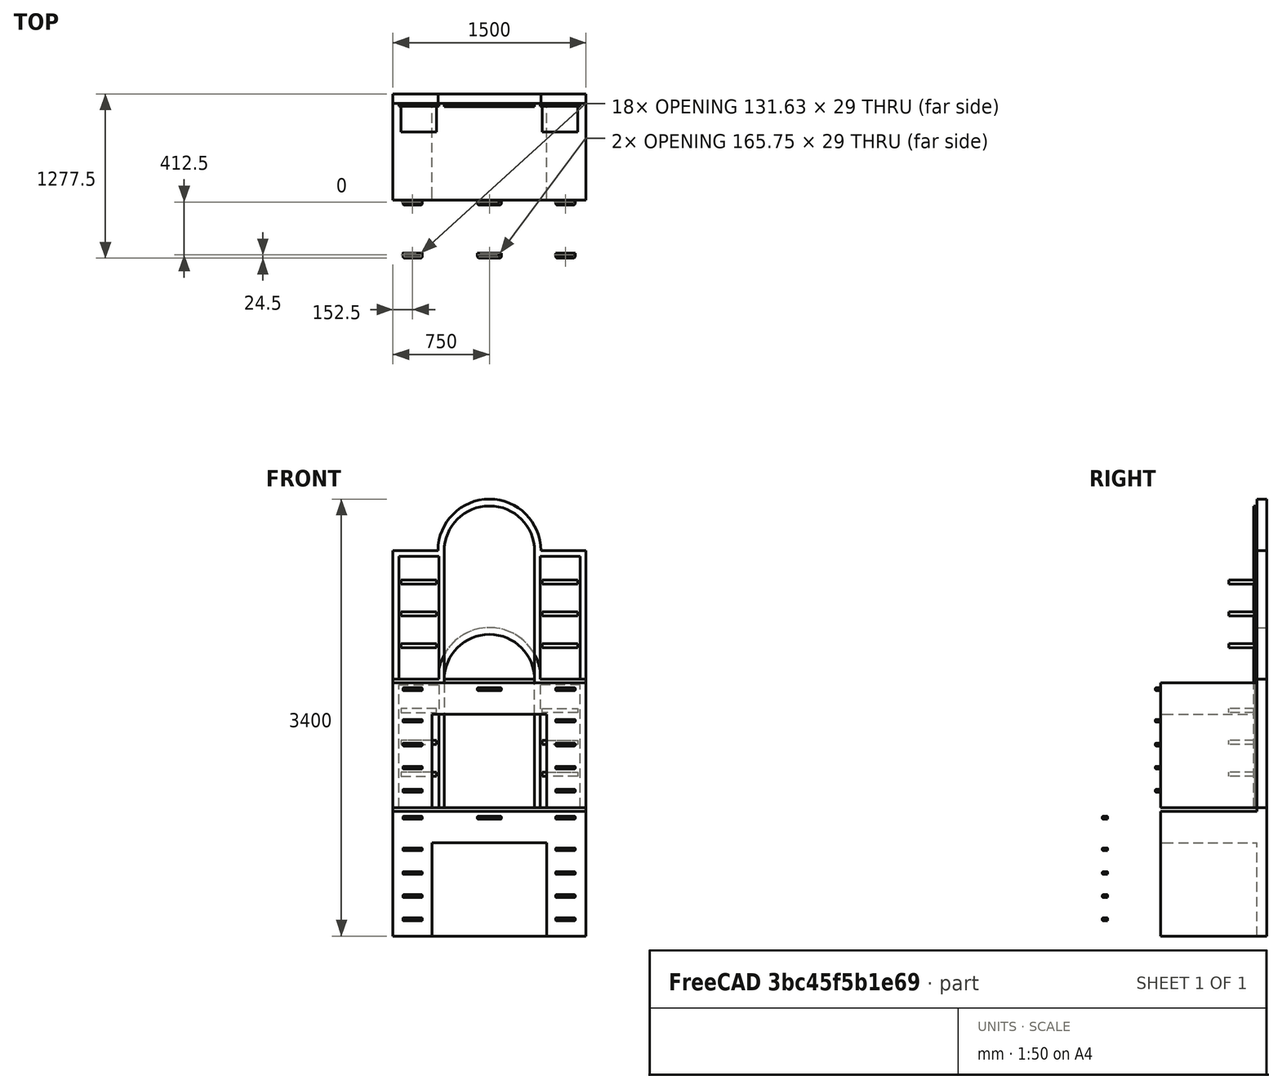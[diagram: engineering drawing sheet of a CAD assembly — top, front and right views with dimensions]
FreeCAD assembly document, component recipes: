
FREECAD ASSEMBLY — COMPONENT RECIPES ("Dressing_Table")

This assembly document has 3 components, labeled P0..P2 below (a component is one placed body or linked part). 3 of them carry a construction recipe — the FreeCAD feature program that regenerates the part from scratch, quoted from this document or its linked companion documents; the rest are supplied as boundary geometry only. No exploded tour is included for this assembly.
COMPONENT P0 — recipe-attached ("Body013", modeled in this document).
Construction recipe (the document's own serialized feature program — sketch geometry with constraints, then the solid features built on it; lengths are millimeters unless a unit is written):

FEATURE [PartDesign::ShapeBinder] CopyPad005
  Placement = pos=(0,-20,9e-15) rot=(0,0,1;0rad)
  TraceSupport = false
FEATURE [PartDesign::Plane] DatumPlane011
  AttachmentSupport = -> [CopyPad005]
  Length = 899.662
  MapMode = 5
  Placement = pos=(0,-95,2.55e-14) rot=(1,0,0;1.5708rad)
  ResizeMode = 0
  Width = 1568.05
FEATURE [Sketcher::SketchObject] Sketch030
  ArcFitTolerance = 1e-06
  AttachmentSupport = -> [CopyPad005]
  ExternalGeometry = -> [CopyPad005]
  FullyConstrained = false
  MakeInternals = false
  MapMode = 5
  Placement = pos=(0,-95,2.55e-14) rot=(1,0,0;1.5708rad)
  sketch-geometry (4):
    g0: LineSegment StartX=-351.618 StartY=995.137 StartZ=0 EndX=-351.618 EndY=0 EndZ=0
    g1: LineSegment StartX=-351.618 StartY=0 StartZ=0 EndX=351.618 EndY=0 EndZ=0
    g2: LineSegment StartX=351.618 StartY=0 StartZ=0 EndX=351.618 EndY=995.137 EndZ=0
    g3: ArcOfCircle CenterX=1.05374e-11 CenterY=995.137 CenterZ=0 NormalX=0 NormalY=0 NormalZ=1 AngleXU=0 Radius=351.618 StartAngle=8.98854e-10 EndAngle=3.14159
  constraints (10):
    c: Coincident(g0,g1)
    c: Coincident(g1,g2)
    c: Vertical(g0)
    c: Vertical(g2)
    c: Horizontal(g1)
    c: Coincident(g0,g-4)
    c: Coincident(g1,g-3)
    c: Coincident(g3,g0)
    c: Coincident(g3,g2)
    c: Tangent(g3,g-5)
FEATURE [PartDesign::Pad] Pad017
  Direction = (0,-1,2e-16)
  Length = 5
  Length2 = 10
  Placement = pos=(0,-20,9e-15) rot=(0,0,1;0rad)
  Profile = -> Sketch030
  ReferenceAxis = -> Sketch030 [N_Axis]
  Refine = true
  Suppressed = false
  Type = 0
FEATURE [PartDesign::Body] Body012
  AllowCompound = false
  Group = -> [DatumPlane011,CopyPad005,Sketch030,Pad017]
  Origin = -> Origin020
  Placement = pos=(0,412.5,0) rot=(0,0,1;0rad)
  Tip = -> Pad017
COMPONENT P1 — recipe-attached ("dressing_table002", modeled in this document).
Construction recipe (the document's own serialized feature program — sketch geometry with constraints, then the solid features built on it; lengths are millimeters unless a unit is written):

FEATURE [Sketcher::SketchObject] Sketch
  ArcFitTolerance = 1e-06
  AttachmentSupport = -> [XZ_Plane]
  FullyConstrained = true
  MakeInternals = false
  MapMode = 5
  Placement = pos=(0,0,0) rot=(1,0,0;1.5708rad)
  sketch-geometry (7):
    g0: LineSegment StartX=-750 StartY=-1000 StartZ=0 EndX=750 EndY=-1000 EndZ=0
    g1: LineSegment StartX=750 StartY=-1000 StartZ=0 EndX=750 EndY=1000 EndZ=0
    g2: LineSegment StartX=750 StartY=1000 StartZ=0 EndX=400 EndY=1000 EndZ=0
    g3: LineSegment StartX=-750 StartY=1000 StartZ=0 EndX=-750 EndY=-1000 EndZ=0
    g4: GeomPoint [constr] X=0 Y=0 Z=0
    g5: ArcOfCircle CenterX=1.35e-14 CenterY=1000 CenterZ=0 NormalX=0 NormalY=0 NormalZ=1 AngleXU=0 Radius=400 StartAngle=0 EndAngle=3.14159
    g6: LineSegment StartX=-400 StartY=1000 StartZ=0 EndX=-750 EndY=1000 EndZ=0
  constraints (18):
    c: Coincident(g0,g1)
    c: Coincident(g1,g2)
    c: Coincident(g6,g3)
    c: Coincident(g3,g0)
    c: Horizontal(g0)
    c: Horizontal(g2)
    c: Vertical(g1)
    c: Vertical(g3)
    c: Symmetric(g2,g0,g4)
    c: Coincident(g4,g-1)
    c: DistanceY(g1,g1) = 2000
    c: DistanceX(g6,g2) = 1500
    c: Symmetric(g1,g6,g5)
    c: Diameter(g5) = 800
    c: Coincident(g5,g6)
    c: Coincident(g5,g2)
    c: Horizontal(g6)
    c: Horizontal(g5,g2)
FEATURE [PartDesign::Pad] Pad
  Direction = (0,-1,2e-16)
  Length = 75
  Length2 = 10
  Placement = pos=(0,0,0) rot=(1,0,0;1.5708rad)
  Profile = -> Sketch
  ReferenceAxis = -> Sketch [N_Axis]
  Refine = true
  Suppressed = false
  Type = 0
FEATURE [Sketcher::SketchObject] Sketch001
  ArcFitTolerance = 1e-06
  AttachmentSupport = -> [Pad]
  FullyConstrained = false
  MakeInternals = false
  MapMode = 5
  Placement = pos=(0,-75,0) rot=(1,0,0;1.5708rad)
  sketch-geometry (14):
    g0: LineSegment [constr] StartX=0 StartY=0 StartZ=0 EndX=936.468 EndY=0 EndZ=0
    g1: LineSegment [constr] StartX=0 StartY=0 StartZ=0 EndX=-879.559 EndY=0 EndZ=0
    g2: ArcOfCircle CenterX=0 CenterY=995.137 CenterZ=0 NormalX=0 NormalY=0 NormalZ=1 AngleXU=0 Radius=351.618 StartAngle=0 EndAngle=3.14159
    g3: LineSegment StartX=-351.618 StartY=995.137 StartZ=0 EndX=-351.618 EndY=0 EndZ=0
    g4: LineSegment StartX=351.618 StartY=995.137 StartZ=0 EndX=351.618 EndY=0 EndZ=0
    g5: LineSegment StartX=-351.618 StartY=0 StartZ=0 EndX=351.618 EndY=0 EndZ=0
    g6: LineSegment StartX=393.332 StartY=955.725 StartZ=0 EndX=393.332 EndY=0 EndZ=0
    g7: LineSegment StartX=393.332 StartY=0 StartZ=0 EndX=704.851 EndY=0 EndZ=0
    g8: LineSegment StartX=704.851 StartY=0 StartZ=0 EndX=704.851 EndY=955.725 EndZ=0
    g9: LineSegment StartX=704.851 StartY=955.725 StartZ=0 EndX=393.332 EndY=955.725 EndZ=0
    g10: LineSegment StartX=-393.332 StartY=955.725 StartZ=0 EndX=-393.332 EndY=0 EndZ=0
    g11: LineSegment StartX=-393.332 StartY=0 StartZ=0 EndX=-704.851 EndY=0 EndZ=0
    g12: LineSegment StartX=-704.851 StartY=0 StartZ=0 EndX=-704.851 EndY=955.725 EndZ=0
    g13: LineSegment StartX=-704.851 StartY=955.725 StartZ=0 EndX=-393.332 EndY=955.725 EndZ=0
  constraints (30):
    c: Coincident(g0,g-1)
    c: Horizontal(g0)
    c: Coincident(g1,g0)
    c: PointOnObject(g1,g-1)
    c: PointOnObject(g2,g-2)
    c: PointOnObject(g3,g1)
    c: Vertical(g3)
    c: PointOnObject(g4,g0)
    c: Vertical(g4)
    c: Tangent(g4,g2) = 1.5708
    c: Tangent(g3,g2) = -1.5708
    c: Coincident(g5,g3)
    c: Coincident(g5,g4)
    c: Coincident(g6,g7)
    c: Coincident(g7,g8)
    c: Coincident(g8,g9)
    c: Coincident(g9,g6)
    c: Vertical(g6)
    c: Vertical(g8)
    c: Horizontal(g7)
    c: Horizontal(g9)
    c: PointOnObject(g7,g0)
    c: Coincident(g10,g11)
    c: Coincident(g11,g12)
    c: Coincident(g12,g13)
    c: Coincident(g13,g10)
    c: Vertical(g10)
    c: Vertical(g12)
    c: Horizontal(g11)
    c: Horizontal(g13)
FEATURE [PartDesign::Pad] Pad001
  BaseFeature = -> Pad
  Direction = (0,-1,2e-16)
  Length = 20
  Length2 = 10
  Placement = pos=(0,0,0) rot=(1,0,0;1.5708rad)
  Profile = -> Sketch001
  ReferenceAxis = -> Sketch001 [N_Axis]
  Refine = true
  Suppressed = false
  Type = 0
FEATURE [Sketcher::SketchObject] Sketch002
  ArcFitTolerance = 1e-06
  AttachmentSupport = -> [Pad001]
  ExternalGeometry = -> [Pad001]
  FullyConstrained = false
  MakeInternals = false
  MapMode = 5
  Placement = pos=(0,-95,2.09e-14) rot=(1,0,0;1.5708rad)
  sketch-geometry (27):
    g0: LineSegment StartX=-686.592 StartY=770.22 StartZ=0 EndX=-686.592 EndY=738.354 EndZ=0
    g1: LineSegment StartX=-686.592 StartY=738.354 StartZ=0 EndX=-411.592 EndY=738.354 EndZ=0
    g2: LineSegment StartX=-411.592 StartY=738.354 StartZ=0 EndX=-411.592 EndY=770.22 EndZ=0
    g3: LineSegment StartX=-411.592 StartY=770.22 StartZ=0 EndX=-686.592 EndY=770.22 EndZ=0
    g4: LineSegment StartX=-686.592 StartY=523.301 StartZ=0 EndX=-686.592 EndY=491.435 EndZ=0
    g5: LineSegment StartX=-686.592 StartY=491.435 StartZ=0 EndX=-411.592 EndY=491.435 EndZ=0
    g6: LineSegment StartX=-411.592 StartY=491.435 StartZ=0 EndX=-411.592 EndY=523.301 EndZ=0
    g7: LineSegment StartX=-411.592 StartY=523.301 StartZ=0 EndX=-686.592 EndY=523.301 EndZ=0
    g8: LineSegment StartX=-686.592 StartY=276.382 StartZ=0 EndX=-686.592 EndY=244.516 EndZ=0
    g9: LineSegment StartX=-686.592 StartY=244.516 StartZ=0 EndX=-411.592 EndY=244.516 EndZ=0
    g10: LineSegment StartX=-411.592 StartY=244.516 StartZ=0 EndX=-411.592 EndY=276.382 EndZ=0
    g11: LineSegment StartX=-411.592 StartY=276.382 StartZ=0 EndX=-686.592 EndY=276.382 EndZ=0
    g12: LineSegment [constr] StartX=-686.592 StartY=738.354 StartZ=0 EndX=-686.592 EndY=523.301 EndZ=0
    g13: LineSegment [constr] StartX=-686.592 StartY=491.435 StartZ=0 EndX=-686.592 EndY=276.382 EndZ=0
    g14: LineSegment [constr] StartX=-549.092 StartY=477.863 StartZ=0 EndX=-549.092 EndY=955.725 EndZ=0
    g15: LineSegment StartX=686.592 StartY=738.354 StartZ=0 EndX=411.592 EndY=738.354 EndZ=0
    g16: LineSegment StartX=411.592 StartY=770.22 StartZ=0 EndX=686.592 EndY=770.22 EndZ=0
    g17: LineSegment StartX=411.592 StartY=738.354 StartZ=0 EndX=411.592 EndY=770.22 EndZ=0
    g18: LineSegment StartX=686.592 StartY=770.22 StartZ=0 EndX=686.592 EndY=738.354 EndZ=0
    g19: LineSegment StartX=411.592 StartY=523.301 StartZ=0 EndX=686.592 EndY=523.301 EndZ=0
    g20: LineSegment StartX=411.592 StartY=491.435 StartZ=0 EndX=411.592 EndY=523.301 EndZ=0
    g21: LineSegment StartX=686.592 StartY=491.435 StartZ=0 EndX=411.592 EndY=491.435 EndZ=0
    g22: LineSegment StartX=686.592 StartY=523.301 StartZ=0 EndX=686.592 EndY=491.435 EndZ=0
    g23: LineSegment StartX=411.592 StartY=244.516 StartZ=0 EndX=411.592 EndY=276.382 EndZ=0
    g24: LineSegment StartX=686.592 StartY=244.516 StartZ=0 EndX=411.592 EndY=244.516 EndZ=0
    g25: LineSegment StartX=411.592 StartY=276.382 StartZ=0 EndX=686.592 EndY=276.382 EndZ=0
    g26: LineSegment StartX=686.592 StartY=276.382 StartZ=0 EndX=686.592 EndY=244.516 EndZ=0
  constraints (66):
    c: Coincident(g0,g1)
    c: Coincident(g1,g2)
    c: Coincident(g2,g3)
    c: Coincident(g3,g0)
    c: Vertical(g0)
    c: Vertical(g2)
    c: Horizontal(g1)
    c: Horizontal(g3)
    c: Coincident(g4,g5)
    c: Coincident(g5,g6)
    c: Coincident(g6,g7)
    c: Coincident(g7,g4)
    c: Vertical(g4)
    c: Vertical(g6)
    c: Horizontal(g5)
    c: Horizontal(g7)
    c: Coincident(g8,g9)
    c: Coincident(g9,g10)
    c: Coincident(g10,g11)
    c: Coincident(g11,g8)
    c: Vertical(g8)
    c: Vertical(g10)
    c: Horizontal(g9)
    c: Horizontal(g11)
    c: Coincident(g12,g0)
    c: Coincident(g12,g4)
    c: Vertical(g12)
    c: Coincident(g13,g4)
    c: Coincident(g13,g8)
    c: Vertical(g13)
    c: Equal(g12,g13)
    c: Equal(g2,g6)
    c: Equal(g6,g10)
    c: Equal(g11,g7)
    c: Equal(g7,g3)
    c: DistanceX(g3,g3) = 275
    c: Symmetric(g2,g0,g14)
    c: Symmetric(g-5,g-5,g14)
    c: Coincident(g18,g15)
    c: Coincident(g15,g17)
    c: Coincident(g17,g16)
    c: Coincident(g16,g18)
    c: Vertical(g18)
    c: Vertical(g17)
    c: Horizontal(g15)
    c: Horizontal(g16)
    c: Coincident(g22,g21)
    c: Coincident(g21,g20)
    c: Coincident(g20,g19)
    c: Coincident(g19,g22)
    c: Vertical(g22)
    c: Vertical(g20)
    c: Horizontal(g21)
    c: Horizontal(g19)
    c: Coincident(g26,g24)
    c: Coincident(g24,g23)
    c: Coincident(g23,g25)
    c: Coincident(g25,g26)
    c: Vertical(g26)
    c: Vertical(g23)
    c: Horizontal(g24)
    c: Horizontal(g25)
    c: Equal(g17,g20)
    c: Equal(g20,g23)
    c: Equal(g25,g19)
    c: Equal(g19,g16)
FEATURE [PartDesign::Pad] Pad002
  BaseFeature = -> Pad001
  Direction = (0,-1,2e-16)
  Length = 200
  Length2 = 10
  Placement = pos=(0,0,0) rot=(1,0,0;1.5708rad)
  Profile = -> Sketch002
  ReferenceAxis = -> Sketch002 [N_Axis]
  Refine = true
  Suppressed = false
  Type = 0
FEATURE [Sketcher::SketchObject] Sketch003
  ArcFitTolerance = 1e-06
  AttachmentSupport = -> [Pad002]
  ExternalGeometry = -> [Pad002]
  FullyConstrained = true
  MakeInternals = false
  MapMode = 5
  Placement = pos=(0,-75,0) rot=(1,0,0;1.5708rad)
  sketch-geometry (4):
    g0: LineSegment StartX=-750 StartY=-1000 StartZ=0 EndX=750 EndY=-1000 EndZ=0
    g1: LineSegment StartX=750 StartY=-1000 StartZ=0 EndX=750 EndY=-30 EndZ=0
    g2: LineSegment StartX=750 StartY=-30 StartZ=0 EndX=-750 EndY=-30 EndZ=0
    g3: LineSegment StartX=-750 StartY=-30 StartZ=0 EndX=-750 EndY=-1000 EndZ=0
  constraints (11):
    c: Coincident(g0,g1)
    c: Coincident(g1,g2)
    c: Coincident(g2,g3)
    c: Coincident(g3,g0)
    c: Horizontal(g0)
    c: Horizontal(g2)
    c: Vertical(g1)
    c: Vertical(g3)
    c: Coincident(g0,g-3)
    c: PointOnObject(g1,g-4)
    c: DistanceY(g1,g1) = 970
FEATURE [PartDesign::Pad] Pad003
  BaseFeature = -> Pad002
  Direction = (0,-1,2e-16)
  Length = 750
  Length2 = 10
  Placement = pos=(0,0,0) rot=(1,0,0;1.5708rad)
  Profile = -> Sketch003
  ReferenceAxis = -> Sketch003 [N_Axis]
  Suppressed = false
  Type = 0
FEATURE [Sketcher::SketchObject] Sketch004
  ArcFitTolerance = 1e-06
  AttachmentSupport = -> [Pad003]
  ExternalGeometry = -> [Pad003]
  FullyConstrained = true
  MakeInternals = false
  MapMode = 5
  Placement = pos=(0,-825,1.897e-13) rot=(1,0,0;1.5708rad)
  sketch-geometry (4):
    g0: LineSegment StartX=-445 StartY=-1000 StartZ=0 EndX=445 EndY=-1000 EndZ=0
    g1: LineSegment StartX=445 StartY=-1000 StartZ=0 EndX=445 EndY=-275 EndZ=0
    g2: LineSegment StartX=445 StartY=-275 StartZ=0 EndX=-445 EndY=-275 EndZ=0
    g3: LineSegment StartX=-445 StartY=-275 StartZ=0 EndX=-445 EndY=-1000 EndZ=0
  constraints (11):
    c: Coincident(g0,g1)
    c: Coincident(g1,g2)
    c: Coincident(g2,g3)
    c: Coincident(g3,g0)
    c: Horizontal(g0)
    c: Vertical(g1)
    c: Vertical(g3)
    c: PointOnObject(g0,g-3)
    c: DistanceX(g2,g2) = 890
    c: DistanceY(g1,g1) = 725
    c: Symmetric(g1,g2,g-2)
FEATURE [PartDesign::Pocket] Pocket
  BaseFeature = -> Pad003
  Direction = (0,1,-2e-16)
  Length = 750
  Length2 = 5
  Placement = pos=(0,0,0) rot=(1,0,0;1.5708rad)
  Profile = -> Sketch004
  ReferenceAxis = -> Sketch004 [N_Axis]
  Suppressed = false
  Type = 0
FEATURE [Sketcher::SketchObject] Sketch005
  ArcFitTolerance = 1e-06
  AttachmentSupport = -> [Pocket]
  ExternalGeometry = -> [Pocket]
  FullyConstrained = true
  MakeInternals = false
  MapMode = 5
  Placement = pos=(0,-825,1.897e-13) rot=(1,0,0;1.5708rad)
  sketch-geometry (24):
    g0: LineSegment StartX=-445 StartY=-275 StartZ=0 EndX=-445 EndY=-30 EndZ=0
    g1: LineSegment StartX=-445 StartY=-30 StartZ=0 EndX=-750 EndY=-30 EndZ=0
    g2: LineSegment StartX=-750 StartY=-30 StartZ=0 EndX=-750 EndY=-275 EndZ=0
    g3: LineSegment StartX=-750 StartY=-275 StartZ=0 EndX=-445 EndY=-275 EndZ=0
    g4: LineSegment StartX=-445 StartY=-460 StartZ=0 EndX=-750 EndY=-460 EndZ=0
    g5: LineSegment StartX=-750 StartY=-460 StartZ=0 EndX=-750 EndY=-640 EndZ=0
    g6: LineSegment StartX=-750 StartY=-640 StartZ=0 EndX=-445 EndY=-640 EndZ=0
    g7: LineSegment StartX=-445 StartY=-640 StartZ=0 EndX=-445 EndY=-460 EndZ=0
    g8: LineSegment StartX=-750 StartY=-820 StartZ=0 EndX=-445 EndY=-820 EndZ=0
    g9: LineSegment StartX=-750 StartY=-820 StartZ=0 EndX=-750 EndY=-1000 EndZ=0
    g10: LineSegment StartX=-750 StartY=-1000 StartZ=0 EndX=-445 EndY=-1000 EndZ=0
    g11: LineSegment StartX=-445 StartY=-1000 StartZ=0 EndX=-445 EndY=-820 EndZ=0
    g12: LineSegment StartX=750 StartY=-30 StartZ=0 EndX=750 EndY=-275 EndZ=0
    g13: LineSegment StartX=445 StartY=-30 StartZ=0 EndX=750 EndY=-30 EndZ=0
    g14: LineSegment StartX=750 StartY=-275 StartZ=0 EndX=445 EndY=-275 EndZ=0
    g15: LineSegment StartX=445 StartY=-460 StartZ=0 EndX=750 EndY=-460 EndZ=0
    g16: LineSegment StartX=750 StartY=-460 StartZ=0 EndX=750 EndY=-640 EndZ=0
    g17: LineSegment StartX=750 StartY=-640 StartZ=0 EndX=445 EndY=-640 EndZ=0
    g18: LineSegment StartX=445 StartY=-640 StartZ=0 EndX=445 EndY=-460 EndZ=0
    g19: LineSegment StartX=445 StartY=-1000 StartZ=0 EndX=445 EndY=-820 EndZ=0
    g20: LineSegment StartX=750 StartY=-1000 StartZ=0 EndX=445 EndY=-1000 EndZ=0
    g21: LineSegment StartX=750 StartY=-820 StartZ=0 EndX=750 EndY=-1000 EndZ=0
    g22: LineSegment StartX=750 StartY=-820 StartZ=0 EndX=445 EndY=-820 EndZ=0
    g23: LineSegment StartX=445 StartY=-30 StartZ=0 EndX=445 EndY=-275 EndZ=0
  constraints (67):
    c: Coincident(g0,g1)
    c: Vertical(g0)
    c: Horizontal(g1)
    c: Coincident(g0,g-6)
    c: Coincident(g1,g2)
    c: PointOnObject(g2,g-5)
    c: Coincident(g2,g3)
    c: Coincident(g3,g0)
    c: Horizontal(g3)
    c: PointOnObject(g4,g-6)
    c: PointOnObject(g4,g-5)
    c: Horizontal(g4)
    c: Coincident(g4,g5)
    c: PointOnObject(g5,g-5)
    c: Coincident(g5,g6)
    c: PointOnObject(g6,g-6)
    c: Horizontal(g6)
    c: Coincident(g6,g7)
    c: PointOnObject(g8,g-5)
    c: PointOnObject(g8,g-6)
    c: Horizontal(g8)
    c: Coincident(g9,g10)
    c: PointOnObject(g10,g-6)
    c: Horizontal(g10)
    c: Coincident(g10,g11)
    c: Coincident(g11,g8)
    c: Coincident(g9,g-5)
    c: DistanceY(g9,g9) = 180
    c: Coincident(g1,g-5)
    c: Horizontal(g13)
    c: Coincident(g13,g12)
    c: Coincident(g12,g14)
    c: Horizontal(g14)
    c: Horizontal(g15)
    c: Coincident(g15,g16)
    c: Coincident(g16,g17)
    c: Horizontal(g17)
    c: Coincident(g17,g18)
    c: Horizontal(g22)
    c: Coincident(g21,g20)
    c: Horizontal(g20)
    c: Coincident(g20,g19)
    c: Coincident(g19,g22)
    c: Coincident(g12,g-4)
    c: Equal(g14,g13)
    c: Horizontal(g15,g4)
    c: Horizontal(g17,g6)
    c: Horizontal(g22,g8)
    c: Horizontal(g19,g10)
    c: Vertical(g15,g17)
    c: Vertical(g17,g22)
    c: Vertical(g22,g19)
    c: Vertical(g19,g14)
    c: Vertical(g21,g20)
    c: Vertical(g20,g12)
    c: Coincident(g23,g13)
    c: Coincident(g23,g14)
    c: Vertical(g23)
    c: Coincident(g14,g-3)
    c: Coincident(g7,g4)
    c: Equal(g5,g9)
    c: Coincident(g18,g15)
    c: Vertical(g15,g12)
    c: Coincident(g22,g21)
    c: Coincident(g9,g8)
    c: DistanceY(g8,g5) = 180
    c: Vertical(g16,g21)
FEATURE [PartDesign::Pad] Pad004
  BaseFeature = -> Pocket
  Direction = (0,-1,2e-16)
  Length = 25
  Length2 = 10
  Placement = pos=(0,0,0) rot=(1,0,0;1.5708rad)
  Profile = -> Sketch005
  ReferenceAxis = -> Sketch005 [N_Axis]
  Reversed = true
  Suppressed = false
  Type = 0
FEATURE [Sketcher::SketchObject] Sketch006
  ArcFitTolerance = 1e-06
  AttachmentSupport = -> [Pad004]
  ExternalGeometry = -> [Pad004]
  FullyConstrained = true
  MakeInternals = false
  MapMode = 5
  Placement = pos=(0,-825,1.897e-13) rot=(1,0,0;1.5708rad)
  sketch-geometry (20):
    g0: LineSegment StartX=-750 StartY=-275 StartZ=0 EndX=-750 EndY=-460 EndZ=0
    g1: LineSegment StartX=-750 StartY=-460 StartZ=0 EndX=-445 EndY=-460 EndZ=0
    g2: LineSegment StartX=-445 StartY=-460 StartZ=0 EndX=-445 EndY=-275 EndZ=0
    g3: LineSegment StartX=-445 StartY=-275 StartZ=0 EndX=-750 EndY=-275 EndZ=0
    g4: LineSegment StartX=-750 StartY=-640 StartZ=0 EndX=-750 EndY=-820 EndZ=0
    g5: LineSegment StartX=-750 StartY=-820 StartZ=0 EndX=-445 EndY=-820 EndZ=0
    g6: LineSegment StartX=-445 StartY=-820 StartZ=0 EndX=-445 EndY=-640 EndZ=0
    g7: LineSegment StartX=-445 StartY=-640 StartZ=0 EndX=-750 EndY=-640 EndZ=0
    g8: LineSegment StartX=445 StartY=-275 StartZ=0 EndX=445 EndY=-460 EndZ=0
    g9: LineSegment StartX=445 StartY=-460 StartZ=0 EndX=750 EndY=-460 EndZ=0
    g10: LineSegment StartX=750 StartY=-460 StartZ=0 EndX=750 EndY=-275 EndZ=0
    g11: LineSegment StartX=750 StartY=-275 StartZ=0 EndX=445 EndY=-275 EndZ=0
    g12: LineSegment StartX=445 StartY=-640 StartZ=0 EndX=445 EndY=-820 EndZ=0
    g13: LineSegment StartX=445 StartY=-820 StartZ=0 EndX=750 EndY=-820 EndZ=0
    g14: LineSegment StartX=750 StartY=-820 StartZ=0 EndX=750 EndY=-640 EndZ=0
    g15: LineSegment StartX=750 StartY=-640 StartZ=0 EndX=445 EndY=-640 EndZ=0
    g16: LineSegment StartX=-445 StartY=-30 StartZ=0 EndX=-445 EndY=-275 EndZ=0
    g17: LineSegment StartX=-445 StartY=-275 StartZ=0 EndX=445 EndY=-275 EndZ=0
    g18: LineSegment StartX=445 StartY=-275 StartZ=0 EndX=445 EndY=-30 EndZ=0
    g19: LineSegment StartX=445 StartY=-30 StartZ=0 EndX=-445 EndY=-30 EndZ=0
  constraints (50):
    c: Coincident(g0,g1)
    c: Coincident(g1,g2)
    c: Coincident(g2,g3)
    c: Coincident(g3,g0)
    c: Vertical(g0)
    c: Vertical(g2)
    c: Horizontal(g1)
    c: Horizontal(g3)
    c: Coincident(g0,g-4)
    c: Coincident(g1,g-3)
    c: Coincident(g4,g5)
    c: Coincident(g5,g6)
    c: Coincident(g6,g7)
    c: Coincident(g7,g4)
    c: Vertical(g4)
    c: Vertical(g6)
    c: Horizontal(g5)
    c: Horizontal(g7)
    c: Coincident(g4,g-6)
    c: Coincident(g5,g-5)
    c: Coincident(g8,g9)
    c: Coincident(g9,g10)
    c: Coincident(g10,g11)
    c: Coincident(g11,g8)
    c: Vertical(g8)
    c: Vertical(g10)
    c: Horizontal(g9)
    c: Horizontal(g11)
    c: Coincident(g8,g-8)
    c: Coincident(g9,g-9)
    c: Coincident(g12,g13)
    c: Coincident(g13,g14)
    c: Coincident(g14,g15)
    c: Coincident(g15,g12)
    c: Vertical(g12)
    c: Vertical(g14)
    c: Horizontal(g13)
    c: Horizontal(g15)
    c: Coincident(g12,g-10)
    c: Coincident(g13,g-11)
    c: Coincident(g16,g17)
    c: Coincident(g17,g18)
    c: Coincident(g18,g19)
    c: Coincident(g19,g16)
    c: Vertical(g16)
    c: Vertical(g18)
    c: Horizontal(g17)
    c: Horizontal(g19)
    c: Coincident(g16,g-7)
    c: Coincident(g17,g8)
FEATURE [PartDesign::Pad] Pad005
  BaseFeature = -> Pad004
  Direction = (0,-1,2e-16)
  Length = 25
  Length2 = 10
  Placement = pos=(0,0,0) rot=(1,0,0;1.5708rad)
  Profile = -> Sketch006
  ReferenceAxis = -> Sketch006 [N_Axis]
  Reversed = true
  Suppressed = false
  Type = 0
FEATURE [PartDesign::Body] Body
  AllowCompound = false
  Group = -> [Sketch,Pad,Sketch001,Pad001,Sketch002,Pad002,Sketch003,Pad003,Sketch004,Pocket,Sketch005,Pad004,Sketch006,Pad005]
  Origin = -> Origin
  Placement = pos=(0,412.5,0) rot=(0,0,1;0rad)
  Tip = -> Pad005
COMPONENT P2 — recipe-attached ("handle_p001", modeled in this document).
Construction recipe (the document's own serialized feature program — sketch geometry with constraints, then the solid features built on it; lengths are millimeters unless a unit is written):

FEATURE [PartDesign::ShapeBinder] CopyPocket001
  Placement = pos=(0,0,0) rot=(1,0,0;1.5708rad)
  TraceSupport = false
FEATURE [PartDesign::Plane] DatumPlane
  AttachmentSupport = -> [CopyPocket001]
  Length = 214.996
  MapMode = 5
  Placement = pos=(0,-825,6.6e-15) rot=(1,0,0;1.5708rad)
  ResizeMode = 0
  Width = 144.392
FEATURE [Sketcher::SketchObject] Sketch008
  ArcFitTolerance = 1e-06
  AttachmentSupport = -> [CopyPocket001]
  ExternalGeometry = -> [CopyPocket001]
  FullyConstrained = true
  MakeInternals = false
  MapMode = 5
  Placement = pos=(0,-825,1.897e-13) rot=(1,0,0;1.5708rad)
  sketch-geometry (4):
    g0: LineSegment StartX=-92.8734 StartY=-68.8715 StartZ=0 EndX=-92.8734 EndY=-90.1429 EndZ=0
    g1: LineSegment StartX=-92.8734 StartY=-90.1429 StartZ=0 EndX=92.8734 EndY=-90.1429 EndZ=0
    g2: LineSegment StartX=92.8734 StartY=-90.1429 StartZ=0 EndX=92.8734 EndY=-68.8715 EndZ=0
    g3: LineSegment StartX=92.8734 StartY=-68.8715 StartZ=0 EndX=-92.8734 EndY=-68.8715 EndZ=0
  constraints (10):
    c: Coincident(g0,g1)
    c: Coincident(g1,g2)
    c: Coincident(g2,g3)
    c: Coincident(g3,g0)
    c: Vertical(g0)
    c: Vertical(g2)
    c: Horizontal(g1)
    c: Horizontal(g3)
    c: Coincident(g0,g-3)
    c: Coincident(g1,g-5)
FEATURE [PartDesign::Pad] Pad006
  Direction = (0,-1,2e-16)
  Length = 40
  Length2 = 10
  Placement = pos=(0,0,0) rot=(1,0,0;1.5708rad)
  Profile = -> Sketch008
  ReferenceAxis = -> Sketch008 [N_Axis]
  Refine = true
  Suppressed = false
  Type = 0
FEATURE [Sketcher::SketchObject] Sketch009
  ArcFitTolerance = 1e-06
  AttachmentSupport = -> [Pad006]
  ExternalGeometry = -> [Pad006]
  FullyConstrained = true
  MakeInternals = false
  MapMode = 5
  Placement = pos=(0,-7.6e-15,-68.8715) rot=(0,0,1;3.14159rad)
  sketch-geometry (4):
    g0: LineSegment StartX=-77.8734 StartY=850 StartZ=0 EndX=-77.8734 EndY=826 EndZ=0
    g1: LineSegment StartX=77.8734 StartY=850 StartZ=0 EndX=77.8734 EndY=826 EndZ=0
    g2: LineSegment StartX=-77.8734 StartY=850 StartZ=0 EndX=77.8734 EndY=850 EndZ=0
    g3: LineSegment StartX=-77.8734 StartY=826 StartZ=0 EndX=77.8734 EndY=826 EndZ=0
  constraints (12):
    c: Coincident(g2,g0)
    c: Coincident(g2,g1)
    c: Horizontal(g2)
    c: DistanceX(g-3,g0) = 15
    c: DistanceX(g1,g-3) = 15
    c: Vertical(g0)
    c: Vertical(g1)
    c: DistanceY(g0,g-4) = 15
    c: DistanceY(g-3,g0) = 1
    c: DistanceY(g-3,g1) = 1
    c: Coincident(g3,g0)
    c: Coincident(g3,g1)
FEATURE [PartDesign::Pocket] Pocket002
  BaseFeature = -> Pad006
  Direction = (0,0,-1)
  Length = 5
  Length2 = 5
  Placement = pos=(0,0,0) rot=(1,0,0;1.5708rad)
  Profile = -> Sketch009
  ReferenceAxis = -> Sketch009 [N_Axis]
  Refine = true
  Suppressed = false
  Type = 1
FEATURE [PartDesign::Fillet] Fillet
  Base = -> Pocket002 [Edge22,Edge21,Edge4,Edge20]
  BaseFeature = -> Pocket002
  Placement = pos=(0,0,0) rot=(1,0,0;1.5708rad)
  Radius = 15
  Refine = true
  SupportTransform = false
  Suppressed = false
  UseAllEdges = false
FEATURE [PartDesign::Fillet] Fillet001
  Base = -> Fillet [Edge8,Edge20,Edge10,Edge26]
  BaseFeature = -> Fillet
  Placement = pos=(0,0,0) rot=(1,0,0;1.5708rad)
  Radius = 5
  Refine = true
  SupportTransform = false
  Suppressed = false
  UseAllEdges = false
FEATURE [PartDesign::Body] Body001
  AllowCompound = false
  Group = -> [DatumPlane,CopyPocket001,Sketch008,Pad006,Sketch009,Pocket002,Fillet,Fillet001]
  Origin = -> Origin005
  Tip = -> Fillet001
FEATURE [PartDesign::ShapeBinder] CopyPocket002
  Placement = pos=(0,0,0) rot=(1,0,0;1.5708rad)
  TraceSupport = false
FEATURE [PartDesign::Plane] DatumPlane001
  AttachmentSupport = -> [CopyPocket002]
  Length = 755.028
  MapMode = 5
  Placement = pos=(0,-825,6.6e-15) rot=(1,0,0;1.5708rad)
  ResizeMode = 0
  Width = 171.855
FEATURE [Sketcher::SketchObject] Sketch010
  ArcFitTolerance = 1e-06
  AttachmentSupport = -> [CopyPocket002]
  ExternalGeometry = -> [CopyPocket002]
  FullyConstrained = true
  MakeInternals = false
  MapMode = 5
  Placement = pos=(0,-825,1.897e-13) rot=(1,0,0;1.5708rad)
  sketch-geometry (4):
    g0: LineSegment StartX=-673.316 StartY=-90.1429 StartZ=0 EndX=-521.684 EndY=-90.1429 EndZ=0
    g1: LineSegment StartX=-521.684 StartY=-90.1429 StartZ=0 EndX=-521.684 EndY=-68.8715 EndZ=0
    g2: LineSegment StartX=-521.684 StartY=-68.8715 StartZ=0 EndX=-673.316 EndY=-68.8715 EndZ=0
    g3: LineSegment StartX=-673.316 StartY=-68.8715 StartZ=0 EndX=-673.316 EndY=-90.1429 EndZ=0
  constraints (10):
    c: Coincident(g0,g1)
    c: Coincident(g1,g2)
    c: Coincident(g2,g3)
    c: Coincident(g3,g0)
    c: Horizontal(g0)
    c: Horizontal(g2)
    c: Vertical(g1)
    c: Vertical(g3)
    c: Coincident(g0,g-4)
    c: Coincident(g1,g-3)
FEATURE [PartDesign::Pad] Pad007
  Direction = (0,-1,2e-16)
  Length = 40
  Length2 = 10
  Placement = pos=(0,0,0) rot=(1,0,0;1.5708rad)
  Profile = -> Sketch010
  ReferenceAxis = -> Sketch010 [N_Axis]
  Refine = true
  Suppressed = false
  Type = 0
FEATURE [Sketcher::SketchObject] Sketch011
  ArcFitTolerance = 1e-06
  AttachmentSupport = -> [Pad007]
  ExternalGeometry = -> [Pad007]
  FullyConstrained = true
  MakeInternals = false
  MapMode = 5
  Placement = pos=(0,-7.6e-15,-68.8715) rot=(0,0,1;3.14159rad)
  sketch-geometry (4):
    g0: LineSegment StartX=536.684 StartY=850 StartZ=0 EndX=536.684 EndY=826 EndZ=0
    g1: LineSegment StartX=536.684 StartY=826 StartZ=0 EndX=658.316 EndY=826 EndZ=0
    g2: LineSegment StartX=658.316 StartY=826 StartZ=0 EndX=658.316 EndY=850 EndZ=0
    g3: LineSegment StartX=658.316 StartY=850 StartZ=0 EndX=536.684 EndY=850 EndZ=0
  constraints (12):
    c: Coincident(g0,g1)
    c: Coincident(g1,g2)
    c: Coincident(g2,g3)
    c: Coincident(g3,g0)
    c: Vertical(g0)
    c: Vertical(g2)
    c: Horizontal(g1)
    c: Horizontal(g3)
    c: DistanceY(g-4,g1) = 1
    c: DistanceX(g1,g-4) = 15
    c: DistanceY(g2,g-4) = 15
    c: DistanceX(g-3,g0) = 15
FEATURE [PartDesign::Pocket] Pocket003
  BaseFeature = -> Pad007
  Direction = (0,0,-1)
  Length = 5
  Length2 = 5
  Placement = pos=(0,0,0) rot=(1,0,0;1.5708rad)
  Profile = -> Sketch011
  ReferenceAxis = -> Sketch011 [N_Axis]
  Refine = true
  Suppressed = false
  Type = 1
FEATURE [PartDesign::Fillet] Fillet002
  Base = -> Pocket003 [Edge19,Edge14,Edge23,Edge11]
  BaseFeature = -> Pocket003
  Placement = pos=(0,0,0) rot=(1,0,0;1.5708rad)
  Radius = 15
  Refine = true
  SupportTransform = false
  Suppressed = false
  UseAllEdges = false
FEATURE [PartDesign::Fillet] Fillet003
  Base = -> Fillet002 [Edge21,Edge4,Edge32,Edge10]
  BaseFeature = -> Fillet002
  Placement = pos=(0,0,0) rot=(1,0,0;1.5708rad)
  Radius = 5
  Refine = true
  SupportTransform = false
  Suppressed = false
  UseAllEdges = false
FEATURE [PartDesign::Body] Body002
  AllowCompound = false
  Group = -> [DatumPlane001,CopyPocket002,Sketch010,Pad007,Sketch011,Pocket003,Fillet002,Fillet003]
  Origin = -> Origin007
  Tip = -> Fillet003
FEATURE [PartDesign::ShapeBinder] CopyPocket003
  Placement = pos=(0,0,0) rot=(1,0,0;1.5708rad)
  TraceSupport = false
FEATURE [PartDesign::Plane] DatumPlane002
  AttachmentSupport = -> [CopyPocket003]
  Length = 798.615
  MapMode = 5
  Placement = pos=(0,-825,6.6e-15) rot=(1,0,0;1.5708rad)
  ResizeMode = 0
  Width = 460.441
FEATURE [Sketcher::SketchObject] Sketch012
  ArcFitTolerance = 1e-06
  AttachmentSupport = -> [CopyPocket003]
  ExternalGeometry = -> [CopyPocket003]
  FullyConstrained = true
  MakeInternals = false
  MapMode = 5
  Placement = pos=(0,-825,1.897e-13) rot=(1,0,0;1.5708rad)
  sketch-geometry (4):
    g0: LineSegment StartX=-673.316 StartY=-313.872 StartZ=0 EndX=-673.316 EndY=-335.143 EndZ=0
    g1: LineSegment StartX=-673.316 StartY=-335.143 StartZ=0 EndX=-521.684 EndY=-335.143 EndZ=0
    g2: LineSegment StartX=-521.684 StartY=-335.143 StartZ=0 EndX=-521.684 EndY=-313.872 EndZ=0
    g3: LineSegment StartX=-521.684 StartY=-313.872 StartZ=0 EndX=-673.316 EndY=-313.872 EndZ=0
  constraints (10):
    c: Coincident(g0,g1)
    c: Coincident(g1,g2)
    c: Coincident(g2,g3)
    c: Coincident(g3,g0)
    c: Vertical(g0)
    c: Vertical(g2)
    c: Horizontal(g1)
    c: Horizontal(g3)
    c: Coincident(g0,g-4)
    c: Coincident(g1,g-3)
FEATURE [PartDesign::Pad] Pad008
  Direction = (0,-1,2e-16)
  Length = 40
  Length2 = 10
  Placement = pos=(0,0,0) rot=(1,0,0;1.5708rad)
  Profile = -> Sketch012
  ReferenceAxis = -> Sketch012 [N_Axis]
  Refine = true
  Suppressed = false
  Type = 0
FEATURE [Sketcher::SketchObject] Sketch013
  ArcFitTolerance = 1e-06
  AttachmentSupport = -> [Pad008]
  ExternalGeometry = -> [Pad008]
  FullyConstrained = true
  MakeInternals = false
  MapMode = 5
  Placement = pos=(0,-3.45e-14,-313.872) rot=(0,0,1;3.14159rad)
  sketch-geometry (4):
    g0: LineSegment StartX=536.684 StartY=850 StartZ=0 EndX=536.684 EndY=826 EndZ=0
    g1: LineSegment StartX=536.684 StartY=826 StartZ=0 EndX=658.316 EndY=826 EndZ=0
    g2: LineSegment StartX=658.316 StartY=826 StartZ=0 EndX=658.316 EndY=850 EndZ=0
    g3: LineSegment StartX=658.316 StartY=850 StartZ=0 EndX=536.684 EndY=850 EndZ=0
  constraints (12):
    c: Coincident(g0,g1)
    c: Coincident(g1,g2)
    c: Coincident(g2,g3)
    c: Coincident(g3,g0)
    c: Vertical(g0)
    c: Vertical(g2)
    c: Horizontal(g1)
    c: Horizontal(g3)
    c: DistanceY(g-4,g1) = 1
    c: DistanceX(g1,g-4) = 15
    c: DistanceY(g0,g-3) = 15
    c: DistanceX(g-3,g0) = 15
FEATURE [PartDesign::Pocket] Pocket004
  BaseFeature = -> Pad008
  Direction = (0,0,-1)
  Length = 5
  Length2 = 5
  Placement = pos=(0,0,0) rot=(1,0,0;1.5708rad)
  Profile = -> Sketch013
  ReferenceAxis = -> Sketch013 [N_Axis]
  Refine = true
  Suppressed = false
  Type = 1
FEATURE [PartDesign::Fillet] Fillet004
  Base = -> Pocket004 [Edge20,Edge4,Edge21,Edge22]
  BaseFeature = -> Pocket004
  Placement = pos=(0,0,0) rot=(1,0,0;1.5708rad)
  Radius = 15
  Refine = true
  SupportTransform = false
  Suppressed = false
  UseAllEdges = false
FEATURE [PartDesign::Fillet] Fillet005
  Base = -> Fillet004 [Edge8,Edge20,Edge10,Edge26]
  BaseFeature = -> Fillet004
  Placement = pos=(0,0,0) rot=(1,0,0;1.5708rad)
  Radius = 5
  Refine = true
  SupportTransform = false
  Suppressed = false
  UseAllEdges = false
FEATURE [PartDesign::Body] Body003
  AllowCompound = false
  Group = -> [DatumPlane002,CopyPocket003,Sketch012,Pad008,Sketch013,Pocket004,Fillet004,Fillet005]
  Origin = -> Origin008
  Tip = -> Fillet005
FEATURE [PartDesign::ShapeBinder] CopyPocket004
  Placement = pos=(0,0,0) rot=(1,0,0;1.5708rad)
  TraceSupport = false
FEATURE [PartDesign::Plane] DatumPlane003
  AttachmentSupport = -> [CopyPocket004]
  Length = 821.715
  MapMode = 5
  Placement = pos=(0,-825,6.6e-15) rot=(1,0,0;1.5708rad)
  ResizeMode = 0
  Width = 668.542
FEATURE [Sketcher::SketchObject] Sketch014
  ArcFitTolerance = 1e-06
  AttachmentSupport = -> [CopyPocket004]
  ExternalGeometry = -> [CopyPocket004]
  FullyConstrained = true
  MakeInternals = false
  MapMode = 5
  Placement = pos=(0,-825,1.897e-13) rot=(1,0,0;1.5708rad)
  sketch-geometry (4):
    g0: LineSegment StartX=-673.316 StartY=-498.872 StartZ=0 EndX=-673.316 EndY=-520.143 EndZ=0
    g1: LineSegment StartX=-673.316 StartY=-520.143 StartZ=0 EndX=-521.684 EndY=-520.143 EndZ=0
    g2: LineSegment StartX=-521.684 StartY=-520.143 StartZ=0 EndX=-521.684 EndY=-498.872 EndZ=0
    g3: LineSegment StartX=-521.684 StartY=-498.872 StartZ=0 EndX=-673.316 EndY=-498.872 EndZ=0
  constraints (10):
    c: Coincident(g0,g1)
    c: Coincident(g1,g2)
    c: Coincident(g2,g3)
    c: Coincident(g3,g0)
    c: Vertical(g0)
    c: Vertical(g2)
    c: Horizontal(g1)
    c: Horizontal(g3)
    c: Coincident(g0,g-3)
    c: Coincident(g1,g-4)
FEATURE [PartDesign::Pad] Pad009
  Direction = (0,-1,2e-16)
  Length = 40
  Length2 = 10
  Placement = pos=(0,0,0) rot=(1,0,0;1.5708rad)
  Profile = -> Sketch014
  ReferenceAxis = -> Sketch014 [N_Axis]
  Refine = true
  Suppressed = false
  Type = 0
FEATURE [Sketcher::SketchObject] Sketch015
  ArcFitTolerance = 1e-06
  AttachmentSupport = -> [Pad009]
  ExternalGeometry = -> [Pad009]
  FullyConstrained = true
  MakeInternals = false
  MapMode = 5
  Placement = pos=(0,-5.49e-14,-498.872) rot=(0,0,1;3.14159rad)
  sketch-geometry (4):
    g0: LineSegment StartX=536.684 StartY=850 StartZ=0 EndX=536.684 EndY=826 EndZ=0
    g1: LineSegment StartX=536.684 StartY=826 StartZ=0 EndX=658.316 EndY=826 EndZ=0
    g2: LineSegment StartX=658.316 StartY=826 StartZ=0 EndX=658.316 EndY=850 EndZ=0
    g3: LineSegment StartX=658.316 StartY=850 StartZ=0 EndX=536.684 EndY=850 EndZ=0
  constraints (12):
    c: Coincident(g0,g1)
    c: Coincident(g1,g2)
    c: Coincident(g2,g3)
    c: Coincident(g3,g0)
    c: Vertical(g0)
    c: Vertical(g2)
    c: Horizontal(g1)
    c: Horizontal(g3)
    c: DistanceX(g1,g-4) = 15
    c: DistanceY(g-4,g1) = 1
    c: DistanceY(g0,g-3) = 15
    c: DistanceX(g-3,g0) = 15
FEATURE [PartDesign::Pocket] Pocket005
  BaseFeature = -> Pad009
  Direction = (0,0,-1)
  Length = 5
  Length2 = 5
  Placement = pos=(0,0,0) rot=(1,0,0;1.5708rad)
  Profile = -> Sketch015
  ReferenceAxis = -> Sketch015 [N_Axis]
  Refine = true
  Suppressed = false
  Type = 1
FEATURE [PartDesign::Fillet] Fillet006
  Base = -> Pocket005 [Edge22,Edge21,Edge4,Edge20]
  BaseFeature = -> Pocket005
  Placement = pos=(0,0,0) rot=(1,0,0;1.5708rad)
  Radius = 15
  Refine = true
  SupportTransform = false
  Suppressed = false
  UseAllEdges = false
FEATURE [PartDesign::Fillet] Fillet007
  Base = -> Fillet006 [Edge10,Edge1,Edge20,Edge4]
  BaseFeature = -> Fillet006
  Placement = pos=(0,0,0) rot=(1,0,0;1.5708rad)
  Radius = 5
  Refine = true
  SupportTransform = false
  Suppressed = false
  UseAllEdges = false
FEATURE [PartDesign::Body] Body004
  AllowCompound = false
  Group = -> [DatumPlane003,CopyPocket004,Sketch014,Pad009,Sketch015,Pocket005,Fillet006,Fillet007]
  Origin = -> Origin009
  Tip = -> Fillet007
FEATURE [PartDesign::ShapeBinder] CopyPocket005
  Placement = pos=(0,0,0) rot=(1,0,0;1.5708rad)
  TraceSupport = false
FEATURE [PartDesign::Plane] DatumPlane004
  AttachmentSupport = -> [CopyPocket005]
  Length = 840.637
  MapMode = 5
  Placement = pos=(0,-825,6.6e-15) rot=(1,0,0;1.5708rad)
  ResizeMode = 0
  Width = 867.464
FEATURE [Sketcher::SketchObject] Sketch016
  ArcFitTolerance = 1e-06
  AttachmentSupport = -> [CopyPocket005]
  ExternalGeometry = -> [CopyPocket005]
  FullyConstrained = true
  MakeInternals = false
  MapMode = 5
  Placement = pos=(0,-825,1.897e-13) rot=(1,0,0;1.5708rad)
  sketch-geometry (4):
    g0: LineSegment StartX=-673.316 StartY=-678.872 StartZ=0 EndX=-673.316 EndY=-700.143 EndZ=0
    g1: LineSegment StartX=-673.316 StartY=-700.143 StartZ=0 EndX=-521.684 EndY=-700.143 EndZ=0
    g2: LineSegment StartX=-521.684 StartY=-700.143 StartZ=0 EndX=-521.684 EndY=-678.872 EndZ=0
    g3: LineSegment StartX=-521.684 StartY=-678.872 StartZ=0 EndX=-673.316 EndY=-678.872 EndZ=0
  constraints (10):
    c: Coincident(g0,g1)
    c: Coincident(g1,g2)
    c: Coincident(g2,g3)
    c: Coincident(g3,g0)
    c: Vertical(g0)
    c: Vertical(g2)
    c: Horizontal(g1)
    c: Horizontal(g3)
    c: Coincident(g0,g-4)
    c: Coincident(g1,g-3)
FEATURE [PartDesign::Pad] Pad010
  Direction = (0,-1,2e-16)
  Length = 40
  Length2 = 10
  Placement = pos=(0,0,0) rot=(1,0,0;1.5708rad)
  Profile = -> Sketch016
  ReferenceAxis = -> Sketch016 [N_Axis]
  Refine = true
  Suppressed = false
  Type = 0
FEATURE [Sketcher::SketchObject] Sketch017
  ArcFitTolerance = 1e-06
  AttachmentSupport = -> [Pad010]
  ExternalGeometry = -> [Pad010]
  FullyConstrained = true
  MakeInternals = false
  MapMode = 5
  Placement = pos=(0,-7.47e-14,-678.872) rot=(0,0,1;3.14159rad)
  sketch-geometry (4):
    g0: LineSegment StartX=536.684 StartY=850 StartZ=0 EndX=536.684 EndY=826 EndZ=0
    g1: LineSegment StartX=536.684 StartY=826 StartZ=0 EndX=658.316 EndY=826 EndZ=0
    g2: LineSegment StartX=658.316 StartY=826 StartZ=0 EndX=658.316 EndY=850 EndZ=0
    g3: LineSegment StartX=658.316 StartY=850 StartZ=0 EndX=536.684 EndY=850 EndZ=0
  constraints (12):
    c: Coincident(g0,g1)
    c: Coincident(g1,g2)
    c: Coincident(g2,g3)
    c: Coincident(g3,g0)
    c: Vertical(g0)
    c: Vertical(g2)
    c: Horizontal(g1)
    c: Horizontal(g3)
    c: DistanceY(g2,g-4) = 15
    c: DistanceX(g1,g-4) = 15
    c: DistanceY(g-4,g1) = 1
    c: DistanceX(g-3,g0) = 15
FEATURE [PartDesign::Pocket] Pocket006
  BaseFeature = -> Pad010
  Direction = (0,0,-1)
  Length = 5
  Length2 = 5
  Placement = pos=(0,0,0) rot=(1,0,0;1.5708rad)
  Profile = -> Sketch017
  ReferenceAxis = -> Sketch017 [N_Axis]
  Refine = true
  Suppressed = false
  Type = 1
FEATURE [PartDesign::Fillet] Fillet008
  Base = -> Pocket006 [Edge4,Edge20,Edge21,Edge22]
  BaseFeature = -> Pocket006
  Placement = pos=(0,0,0) rot=(1,0,0;1.5708rad)
  Radius = 15
  Refine = true
  SupportTransform = false
  Suppressed = false
  UseAllEdges = false
FEATURE [PartDesign::Fillet] Fillet009
  Base = -> Fillet008 [Edge8,Edge10,Edge26,Edge20]
  BaseFeature = -> Fillet008
  Placement = pos=(0,0,0) rot=(1,0,0;1.5708rad)
  Radius = 5
  Refine = true
  SupportTransform = false
  Suppressed = false
  UseAllEdges = false
FEATURE [PartDesign::Body] Body005
  AllowCompound = false
  Group = -> [DatumPlane004,CopyPocket005,Sketch016,Pad010,Sketch017,Pocket006,Fillet008,Fillet009]
  Origin = -> Origin010
  Tip = -> Fillet009
FEATURE [PartDesign::ShapeBinder] CopyPocket006
  Placement = pos=(0,0,0) rot=(1,0,0;1.5708rad)
  TraceSupport = false
FEATURE [PartDesign::Plane] DatumPlane005
  AttachmentSupport = -> [CopyPocket006]
  Length = 857.323
  MapMode = 5
  Placement = pos=(0,-825,6.6e-15) rot=(1,0,0;1.5708rad)
  ResizeMode = 0
  Width = 1064.15
FEATURE [Sketcher::SketchObject] Sketch018
  ArcFitTolerance = 1e-06
  AttachmentSupport = -> [CopyPocket006]
  ExternalGeometry = -> [CopyPocket006]
  FullyConstrained = true
  MakeInternals = false
  MapMode = 5
  Placement = pos=(0,-825,1.897e-13) rot=(1,0,0;1.5708rad)
  sketch-geometry (4):
    g0: LineSegment StartX=-673.316 StartY=-858.872 StartZ=0 EndX=-673.316 EndY=-880.143 EndZ=0
    g1: LineSegment StartX=-673.316 StartY=-880.143 StartZ=0 EndX=-521.684 EndY=-880.143 EndZ=0
    g2: LineSegment StartX=-521.684 StartY=-880.143 StartZ=0 EndX=-521.684 EndY=-858.872 EndZ=0
    g3: LineSegment StartX=-521.684 StartY=-858.872 StartZ=0 EndX=-673.316 EndY=-858.872 EndZ=0
  constraints (10):
    c: Coincident(g0,g1)
    c: Coincident(g1,g2)
    c: Coincident(g2,g3)
    c: Coincident(g3,g0)
    c: Vertical(g0)
    c: Vertical(g2)
    c: Horizontal(g1)
    c: Horizontal(g3)
    c: Coincident(g0,g-3)
    c: Coincident(g1,g-4)
FEATURE [PartDesign::Pad] Pad011
  Direction = (0,-1,2e-16)
  Length = 40
  Length2 = 10
  Placement = pos=(0,0,0) rot=(1,0,0;1.5708rad)
  Profile = -> Sketch018
  ReferenceAxis = -> Sketch018 [N_Axis]
  Refine = true
  Suppressed = false
  Type = 0
FEATURE [Sketcher::SketchObject] Sketch019
  ArcFitTolerance = 1e-06
  AttachmentSupport = -> [Pad011]
  ExternalGeometry = -> [Pad011]
  FullyConstrained = true
  MakeInternals = false
  MapMode = 5
  Placement = pos=(0,-9.45e-14,-858.872) rot=(0,0,1;3.14159rad)
  sketch-geometry (4):
    g0: LineSegment StartX=536.684 StartY=850 StartZ=0 EndX=536.684 EndY=826 EndZ=0
    g1: LineSegment StartX=536.684 StartY=826 StartZ=0 EndX=658.316 EndY=826 EndZ=0
    g2: LineSegment StartX=658.316 StartY=826 StartZ=0 EndX=658.316 EndY=850 EndZ=0
    g3: LineSegment StartX=658.316 StartY=850 StartZ=0 EndX=536.684 EndY=850 EndZ=0
  constraints (12):
    c: Coincident(g0,g1)
    c: Coincident(g1,g2)
    c: Coincident(g2,g3)
    c: Coincident(g3,g0)
    c: Vertical(g0)
    c: Vertical(g2)
    c: Horizontal(g1)
    c: Horizontal(g3)
    c: DistanceX(g1,g-4) = 15
    c: DistanceY(g2,g-4) = 15
    c: DistanceX(g-3,g0) = 15
    c: DistanceY(g-4,g1) = 1
FEATURE [PartDesign::Pocket] Pocket007
  BaseFeature = -> Pad011
  Direction = (0,0,-1)
  Length = 1
  Length2 = 5
  Placement = pos=(0,0,0) rot=(1,0,0;1.5708rad)
  Profile = -> Sketch019
  ReferenceAxis = -> Sketch019 [N_Axis]
  Refine = true
  Suppressed = false
  Type = 1
FEATURE [PartDesign::Fillet] Fillet010
  Base = -> Pocket007 [Edge4,Edge20,Edge22,Edge21]
  BaseFeature = -> Pocket007
  Placement = pos=(0,0,0) rot=(1,0,0;1.5708rad)
  Radius = 15
  Refine = true
  SupportTransform = false
  Suppressed = false
  UseAllEdges = false
FEATURE [PartDesign::Fillet] Fillet011
  Base = -> Fillet010 [Edge10,Edge26,Edge8,Edge20]
  BaseFeature = -> Fillet010
  Placement = pos=(0,0,0) rot=(1,0,0;1.5708rad)
  Radius = 5
  Refine = true
  SupportTransform = false
  Suppressed = false
  UseAllEdges = false
FEATURE [PartDesign::Body] Body006
  AllowCompound = false
  Group = -> [DatumPlane005,CopyPocket006,Sketch018,Pad011,Sketch019,Pocket007,Fillet010,Fillet011]
  Origin = -> Origin011
  Tip = -> Fillet011
FEATURE [PartDesign::ShapeBinder] CopyPocket007
  Placement = pos=(0,0,0) rot=(1,0,0;1.5708rad)
  TraceSupport = false
FEATURE [PartDesign::Plane] DatumPlane006
  AttachmentSupport = -> [CopyPocket007]
  Length = 748.322
  MapMode = 5
  Placement = pos=(0,-825,6.6e-15) rot=(1,0,0;1.5708rad)
  ResizeMode = 0
  Width = 171.593
FEATURE [Sketcher::SketchObject] Sketch020
  ArcFitTolerance = 1e-06
  AttachmentSupport = -> [CopyPocket007]
  ExternalGeometry = -> [CopyPocket007]
  FullyConstrained = true
  MakeInternals = false
  MapMode = 5
  Placement = pos=(0,-825,1.897e-13) rot=(1,0,0;1.5708rad)
  sketch-geometry (4):
    g0: LineSegment StartX=515.24 StartY=-68.8715 StartZ=0 EndX=515.24 EndY=-90.1429 EndZ=0
    g1: LineSegment StartX=515.24 StartY=-90.1429 StartZ=0 EndX=666.872 EndY=-90.1429 EndZ=0
    g2: LineSegment StartX=666.872 StartY=-90.1429 StartZ=0 EndX=666.872 EndY=-68.8715 EndZ=0
    g3: LineSegment StartX=666.872 StartY=-68.8715 StartZ=0 EndX=515.24 EndY=-68.8715 EndZ=0
  constraints (10):
    c: Coincident(g0,g1)
    c: Coincident(g1,g2)
    c: Coincident(g2,g3)
    c: Coincident(g3,g0)
    c: Vertical(g0)
    c: Vertical(g2)
    c: Horizontal(g1)
    c: Horizontal(g3)
    c: Coincident(g0,g-3)
    c: Coincident(g1,g-4)
FEATURE [PartDesign::Pad] Pad012
  Direction = (0,-1,2e-16)
  Length = 40
  Length2 = 10
  Placement = pos=(0,0,0) rot=(1,0,0;1.5708rad)
  Profile = -> Sketch020
  ReferenceAxis = -> Sketch020 [N_Axis]
  Refine = true
  Suppressed = false
  Type = 0
FEATURE [Sketcher::SketchObject] Sketch021
  ArcFitTolerance = 1e-06
  AttachmentSupport = -> [Pad012]
  ExternalGeometry = -> [Pad012]
  FullyConstrained = true
  MakeInternals = false
  MapMode = 5
  Placement = pos=(0,-7.6e-15,-68.8715) rot=(0,0,1;3.14159rad)
  sketch-geometry (4):
    g0: LineSegment StartX=-651.872 StartY=850 StartZ=0 EndX=-651.872 EndY=826 EndZ=0
    g1: LineSegment StartX=-651.872 StartY=826 StartZ=0 EndX=-530.24 EndY=826 EndZ=0
    g2: LineSegment StartX=-530.24 StartY=826 StartZ=0 EndX=-530.24 EndY=850 EndZ=0
    g3: LineSegment StartX=-530.24 StartY=850 StartZ=0 EndX=-651.872 EndY=850 EndZ=0
  constraints (12):
    c: Coincident(g0,g1)
    c: Coincident(g1,g2)
    c: Coincident(g2,g3)
    c: Coincident(g3,g0)
    c: Vertical(g0)
    c: Vertical(g2)
    c: Horizontal(g1)
    c: Horizontal(g3)
    c: DistanceX(g2,g-4) = 15
    c: DistanceX(g-3,g0) = 15
    c: DistanceY(g-3,g0) = 1
    c: DistanceY(g2,g-4) = 15
FEATURE [PartDesign::Pocket] Pocket008
  BaseFeature = -> Pad012
  Direction = (0,0,-1)
  Length = 5
  Length2 = 5
  Placement = pos=(0,0,0) rot=(1,0,0;1.5708rad)
  Profile = -> Sketch021
  ReferenceAxis = -> Sketch021 [N_Axis]
  Refine = true
  Suppressed = false
  Type = 1
FEATURE [PartDesign::Fillet] Fillet012
  Base = -> Pocket008 [Edge4,Edge20,Edge21,Edge22]
  BaseFeature = -> Pocket008
  Placement = pos=(0,0,0) rot=(1,0,0;1.5708rad)
  Radius = 15
  Refine = true
  SupportTransform = false
  Suppressed = false
  UseAllEdges = false
FEATURE [PartDesign::Fillet] Fillet013
  Base = -> Fillet012 [Edge10,Edge26,Edge8,Edge20]
  BaseFeature = -> Fillet012
  Placement = pos=(0,0,0) rot=(1,0,0;1.5708rad)
  Radius = 5
  Refine = true
  SupportTransform = false
  Suppressed = false
  UseAllEdges = false
FEATURE [PartDesign::Body] Body007
  AllowCompound = false
  Group = -> [DatumPlane006,CopyPocket007,Sketch020,Pad012,Sketch021,Pocket008,Fillet012,Fillet013]
  Origin = -> Origin012
  Tip = -> Fillet013
FEATURE [PartDesign::ShapeBinder] CopyPocket008
  Placement = pos=(0,0,0) rot=(1,0,0;1.5708rad)
  TraceSupport = false
FEATURE [PartDesign::Plane] DatumPlane007
  AttachmentSupport = -> [CopyPocket008]
  Length = 791.707
  MapMode = 5
  Placement = pos=(0,-825,6.6e-15) rot=(1,0,0;1.5708rad)
  ResizeMode = 0
  Width = 459.977
FEATURE [Sketcher::SketchObject] Sketch022
  ArcFitTolerance = 1e-06
  AttachmentSupport = -> [CopyPocket008]
  ExternalGeometry = -> [CopyPocket008]
  FullyConstrained = true
  MakeInternals = false
  MapMode = 5
  Placement = pos=(0,-825,1.897e-13) rot=(1,0,0;1.5708rad)
  sketch-geometry (4):
    g0: LineSegment StartX=515.24 StartY=-313.872 StartZ=0 EndX=515.24 EndY=-335.143 EndZ=0
    g1: LineSegment StartX=515.24 StartY=-335.143 StartZ=0 EndX=666.872 EndY=-335.143 EndZ=0
    g2: LineSegment StartX=666.872 StartY=-335.143 StartZ=0 EndX=666.872 EndY=-313.872 EndZ=0
    g3: LineSegment StartX=666.872 StartY=-313.872 StartZ=0 EndX=515.24 EndY=-313.872 EndZ=0
  constraints (10):
    c: Coincident(g0,g1)
    c: Coincident(g1,g2)
    c: Coincident(g2,g3)
    c: Coincident(g3,g0)
    c: Vertical(g0)
    c: Vertical(g2)
    c: Horizontal(g1)
    c: Horizontal(g3)
    c: Coincident(g0,g-3)
    c: Coincident(g1,g-4)
FEATURE [PartDesign::Pad] Pad013
  Direction = (0,-1,2e-16)
  Length = 40
  Length2 = 10
  Placement = pos=(0,0,0) rot=(1,0,0;1.5708rad)
  Profile = -> Sketch022
  ReferenceAxis = -> Sketch022 [N_Axis]
  Refine = true
  Suppressed = false
  Type = 0
FEATURE [Sketcher::SketchObject] Sketch023
  ArcFitTolerance = 1e-06
  AttachmentSupport = -> [Pad013]
  ExternalGeometry = -> [Pad013]
  FullyConstrained = true
  MakeInternals = false
  MapMode = 5
  Placement = pos=(0,-3.45e-14,-313.872) rot=(0,0,1;3.14159rad)
  sketch-geometry (4):
    g0: LineSegment StartX=-651.872 StartY=850 StartZ=0 EndX=-651.872 EndY=826 EndZ=0
    g1: LineSegment StartX=-651.872 StartY=826 StartZ=0 EndX=-530.24 EndY=826 EndZ=0
    g2: LineSegment StartX=-530.24 StartY=826 StartZ=0 EndX=-530.24 EndY=850 EndZ=0
    g3: LineSegment StartX=-530.24 StartY=850 StartZ=0 EndX=-651.872 EndY=850 EndZ=0
  constraints (12):
    c: Coincident(g0,g1)
    c: Coincident(g1,g2)
    c: Coincident(g2,g3)
    c: Coincident(g3,g0)
    c: Vertical(g0)
    c: Vertical(g2)
    c: Horizontal(g1)
    c: Horizontal(g3)
    c: DistanceX(g2,g-4) = 15
    c: DistanceY(g2,g-4) = 15
    c: DistanceY(g-4,g1) = 1
    c: DistanceX(g-3,g0) = 15
FEATURE [PartDesign::Pocket] Pocket009
  BaseFeature = -> Pad013
  Direction = (0,0,-1)
  Length = 5
  Length2 = 5
  Placement = pos=(0,0,0) rot=(1,0,0;1.5708rad)
  Profile = -> Sketch023
  ReferenceAxis = -> Sketch023 [N_Axis]
  Refine = true
  Suppressed = false
  Type = 1
FEATURE [PartDesign::Fillet] Fillet014
  Base = -> Pocket009 [Edge4,Edge20,Edge21,Edge22]
  BaseFeature = -> Pocket009
  Placement = pos=(0,0,0) rot=(1,0,0;1.5708rad)
  Radius = 15
  Refine = true
  SupportTransform = false
  Suppressed = false
  UseAllEdges = false
FEATURE [PartDesign::Fillet] Fillet015
  Base = -> Fillet014 [Edge10,Edge26,Edge8,Edge20]
  BaseFeature = -> Fillet014
  Placement = pos=(0,0,0) rot=(1,0,0;1.5708rad)
  Radius = 5
  Refine = true
  SupportTransform = false
  Suppressed = false
  UseAllEdges = false
FEATURE [PartDesign::Body] Body008
  AllowCompound = false
  Group = -> [DatumPlane007,CopyPocket008,Sketch022,Pad013,Sketch023,Pocket009,Fillet014,Fillet015]
  Origin = -> Origin013
  Tip = -> Fillet015
FEATURE [PartDesign::ShapeBinder] CopyPocket009
  Placement = pos=(0,0,0) rot=(1,0,0;1.5708rad)
  TraceSupport = false
FEATURE [PartDesign::Plane] DatumPlane008
  AttachmentSupport = -> [CopyPocket009]
  Length = 814.7
  MapMode = 5
  Placement = pos=(0,-825,6.6e-15) rot=(1,0,0;1.5708rad)
  ResizeMode = 0
  Width = 667.971
FEATURE [Sketcher::SketchObject] Sketch024
  ArcFitTolerance = 1e-06
  AttachmentSupport = -> [CopyPocket009]
  ExternalGeometry = -> [CopyPocket009]
  FullyConstrained = true
  MakeInternals = false
  MapMode = 5
  Placement = pos=(0,-825,1.897e-13) rot=(1,0,0;1.5708rad)
  sketch-geometry (4):
    g0: LineSegment StartX=515.24 StartY=-498.872 StartZ=0 EndX=515.24 EndY=-520.143 EndZ=0
    g1: LineSegment StartX=515.24 StartY=-520.143 StartZ=0 EndX=666.872 EndY=-520.143 EndZ=0
    g2: LineSegment StartX=666.872 StartY=-520.143 StartZ=0 EndX=666.872 EndY=-498.872 EndZ=0
    g3: LineSegment StartX=666.872 StartY=-498.872 StartZ=0 EndX=515.24 EndY=-498.872 EndZ=0
  constraints (10):
    c: Coincident(g0,g1)
    c: Coincident(g1,g2)
    c: Coincident(g2,g3)
    c: Coincident(g3,g0)
    c: Vertical(g0)
    c: Vertical(g2)
    c: Horizontal(g1)
    c: Horizontal(g3)
    c: Coincident(g0,g-3)
    c: Coincident(g1,g-4)
FEATURE [PartDesign::Pad] Pad014
  Direction = (0,-1,2e-16)
  Length = 40
  Length2 = 10
  Placement = pos=(0,0,0) rot=(1,0,0;1.5708rad)
  Profile = -> Sketch024
  ReferenceAxis = -> Sketch024 [N_Axis]
  Refine = true
  Suppressed = false
  Type = 0
FEATURE [Sketcher::SketchObject] Sketch025
  ArcFitTolerance = 1e-06
  AttachmentSupport = -> [Pad014]
  ExternalGeometry = -> [Pad014]
  FullyConstrained = true
  MakeInternals = false
  MapMode = 5
  Placement = pos=(0,-5.49e-14,-498.872) rot=(0,0,1;3.14159rad)
  sketch-geometry (4):
    g0: LineSegment StartX=-651.872 StartY=850 StartZ=0 EndX=-651.872 EndY=826 EndZ=0
    g1: LineSegment StartX=-651.872 StartY=826 StartZ=0 EndX=-530.24 EndY=826 EndZ=0
    g2: LineSegment StartX=-530.24 StartY=826 StartZ=0 EndX=-530.24 EndY=850 EndZ=0
    g3: LineSegment StartX=-530.24 StartY=850 StartZ=0 EndX=-651.872 EndY=850 EndZ=0
  constraints (12):
    c: Coincident(g0,g1)
    c: Coincident(g1,g2)
    c: Coincident(g2,g3)
    c: Coincident(g3,g0)
    c: Vertical(g0)
    c: Vertical(g2)
    c: Horizontal(g1)
    c: Horizontal(g3)
    c: DistanceX(g2,g-4) = 15
    c: DistanceY(g2,g-4) = 15
    c: DistanceY(g-4,g1) = 1
    c: DistanceX(g-3,g0) = 15
FEATURE [PartDesign::Pocket] Pocket010
  BaseFeature = -> Pad014
  Direction = (0,0,-1)
  Length = 5
  Length2 = 5
  Placement = pos=(0,0,0) rot=(1,0,0;1.5708rad)
  Profile = -> Sketch025
  ReferenceAxis = -> Sketch025 [N_Axis]
  Refine = true
  Suppressed = false
  Type = 1
FEATURE [PartDesign::Fillet] Fillet016
  Base = -> Pocket010 [Edge20,Edge4,Edge22,Edge21]
  BaseFeature = -> Pocket010
  Placement = pos=(0,0,0) rot=(1,0,0;1.5708rad)
  Radius = 15
  Refine = true
  SupportTransform = false
  Suppressed = false
  UseAllEdges = false
FEATURE [PartDesign::Fillet] Fillet017
  Base = -> Fillet016 [Edge10,Edge8,Edge26,Edge20]
  BaseFeature = -> Fillet016
  Placement = pos=(0,0,0) rot=(1,0,0;1.5708rad)
  Radius = 5
  Refine = true
  SupportTransform = false
  Suppressed = false
  UseAllEdges = false
FEATURE [PartDesign::Body] Body009
  AllowCompound = false
  Group = -> [DatumPlane008,CopyPocket009,Sketch024,Pad014,Sketch025,Pocket010,Fillet016,Fillet017]
  Origin = -> Origin014
  Tip = -> Fillet017
FEATURE [PartDesign::ShapeBinder] CopyPocket010
  Placement = pos=(0,0,0) rot=(1,0,0;1.5708rad)
  TraceSupport = false
FEATURE [PartDesign::Plane] DatumPlane009
  AttachmentSupport = -> [CopyPocket010]
  Length = 833.535
  MapMode = 5
  Placement = pos=(0,-825,6.6e-15) rot=(1,0,0;1.5708rad)
  ResizeMode = 0
  Width = 866.806
FEATURE [Sketcher::SketchObject] Sketch026
  ArcFitTolerance = 1e-06
  AttachmentSupport = -> [CopyPocket010]
  ExternalGeometry = -> [CopyPocket010]
  FullyConstrained = true
  MakeInternals = false
  MapMode = 5
  Placement = pos=(0,-825,1.897e-13) rot=(1,0,0;1.5708rad)
  sketch-geometry (4):
    g0: LineSegment StartX=515.24 StartY=-678.872 StartZ=0 EndX=515.24 EndY=-700.143 EndZ=0
    g1: LineSegment StartX=515.24 StartY=-700.143 StartZ=0 EndX=666.872 EndY=-700.143 EndZ=0
    g2: LineSegment StartX=666.872 StartY=-700.143 StartZ=0 EndX=666.872 EndY=-678.872 EndZ=0
    g3: LineSegment StartX=666.872 StartY=-678.872 StartZ=0 EndX=515.24 EndY=-678.872 EndZ=0
  constraints (10):
    c: Coincident(g0,g1)
    c: Coincident(g1,g2)
    c: Coincident(g2,g3)
    c: Coincident(g3,g0)
    c: Vertical(g0)
    c: Vertical(g2)
    c: Horizontal(g1)
    c: Horizontal(g3)
    c: Coincident(g0,g-3)
    c: Coincident(g1,g-4)
FEATURE [PartDesign::Pad] Pad015
  Direction = (0,-1,2e-16)
  Length = 40
  Length2 = 10
  Placement = pos=(0,0,0) rot=(1,0,0;1.5708rad)
  Profile = -> Sketch026
  ReferenceAxis = -> Sketch026 [N_Axis]
  Refine = true
  Suppressed = false
  Type = 0
FEATURE [Sketcher::SketchObject] Sketch027
  ArcFitTolerance = 1e-06
  AttachmentSupport = -> [Pad015]
  ExternalGeometry = -> [Pad015]
  FullyConstrained = true
  MakeInternals = false
  MapMode = 5
  Placement = pos=(0,-7.47e-14,-678.872) rot=(0,0,1;3.14159rad)
  sketch-geometry (4):
    g0: LineSegment StartX=-651.872 StartY=850 StartZ=0 EndX=-651.872 EndY=826 EndZ=0
    g1: LineSegment StartX=-651.872 StartY=826 StartZ=0 EndX=-530.24 EndY=826 EndZ=0
    g2: LineSegment StartX=-530.24 StartY=826 StartZ=0 EndX=-530.24 EndY=850 EndZ=0
    g3: LineSegment StartX=-530.24 StartY=850 StartZ=0 EndX=-651.872 EndY=850 EndZ=0
  constraints (12):
    c: Coincident(g0,g1)
    c: Coincident(g1,g2)
    c: Coincident(g2,g3)
    c: Coincident(g3,g0)
    c: Vertical(g0)
    c: Vertical(g2)
    c: Horizontal(g1)
    c: Horizontal(g3)
    c: DistanceX(g-3,g0) = 15
    c: DistanceY(g2,g-4) = 15
    c: DistanceX(g2,g-4) = 15
    c: DistanceY(g-4,g1) = 1
FEATURE [PartDesign::Pocket] Pocket011
  BaseFeature = -> Pad015
  Direction = (0,0,-1)
  Length = 5
  Length2 = 5
  Placement = pos=(0,0,0) rot=(1,0,0;1.5708rad)
  Profile = -> Sketch027
  ReferenceAxis = -> Sketch027 [N_Axis]
  Refine = true
  Suppressed = false
  Type = 1
FEATURE [PartDesign::Fillet] Fillet018
  Base = -> Pocket011 [Edge4,Edge20,Edge21,Edge22]
  BaseFeature = -> Pocket011
  Placement = pos=(0,0,0) rot=(1,0,0;1.5708rad)
  Radius = 15
  Refine = true
  SupportTransform = false
  Suppressed = false
  UseAllEdges = false
FEATURE [PartDesign::Fillet] Fillet019
  Base = -> Fillet018 [Edge10,Edge26,Edge8,Edge20]
  BaseFeature = -> Fillet018
  Placement = pos=(0,0,0) rot=(1,0,0;1.5708rad)
  Radius = 5
  Refine = true
  SupportTransform = false
  Suppressed = false
  UseAllEdges = false
FEATURE [PartDesign::Body] Body010
  AllowCompound = false
  Group = -> [DatumPlane009,CopyPocket010,Sketch026,Pad015,Sketch027,Pocket011,Fillet018,Fillet019]
  Origin = -> Origin015
  Tip = -> Fillet019
FEATURE [PartDesign::ShapeBinder] CopyPocket011
  Placement = pos=(0,0,0) rot=(1,0,0;1.5708rad)
  TraceSupport = false
FEATURE [PartDesign::Plane] DatumPlane010
  AttachmentSupport = -> [CopyPocket011]
  Length = 850.143
  MapMode = 5
  Placement = pos=(0,-825,6.6e-15) rot=(1,0,0;1.5708rad)
  ResizeMode = 0
  Width = 1063.41
FEATURE [Sketcher::SketchObject] Sketch028
  ArcFitTolerance = 1e-06
  AttachmentSupport = -> [CopyPocket011]
  ExternalGeometry = -> [CopyPocket011]
  FullyConstrained = true
  MakeInternals = false
  MapMode = 5
  Placement = pos=(0,-825,1.897e-13) rot=(1,0,0;1.5708rad)
  sketch-geometry (4):
    g0: LineSegment StartX=515.24 StartY=-858.872 StartZ=0 EndX=515.24 EndY=-880.143 EndZ=0
    g1: LineSegment StartX=515.24 StartY=-880.143 StartZ=0 EndX=666.872 EndY=-880.143 EndZ=0
    g2: LineSegment StartX=666.872 StartY=-880.143 StartZ=0 EndX=666.872 EndY=-858.872 EndZ=0
    g3: LineSegment StartX=666.872 StartY=-858.872 StartZ=0 EndX=515.24 EndY=-858.872 EndZ=0
  constraints (10):
    c: Coincident(g0,g1)
    c: Coincident(g1,g2)
    c: Coincident(g2,g3)
    c: Coincident(g3,g0)
    c: Vertical(g0)
    c: Vertical(g2)
    c: Horizontal(g1)
    c: Horizontal(g3)
    c: Coincident(g0,g-3)
    c: Coincident(g1,g-4)
FEATURE [PartDesign::Pad] Pad016
  Direction = (0,-1,2e-16)
  Length = 40
  Length2 = 10
  Placement = pos=(0,0,0) rot=(1,0,0;1.5708rad)
  Profile = -> Sketch028
  ReferenceAxis = -> Sketch028 [N_Axis]
  Refine = true
  Suppressed = false
  Type = 0
FEATURE [Sketcher::SketchObject] Sketch029
  ArcFitTolerance = 1e-06
  AttachmentSupport = -> [Pad016]
  ExternalGeometry = -> [Pad016]
  FullyConstrained = true
  MakeInternals = false
  MapMode = 5
  Placement = pos=(0,-9.45e-14,-858.872) rot=(0,0,1;3.14159rad)
  sketch-geometry (4):
    g0: LineSegment StartX=-651.872 StartY=850 StartZ=0 EndX=-651.872 EndY=826 EndZ=0
    g1: LineSegment StartX=-651.872 StartY=826 StartZ=0 EndX=-530.24 EndY=826 EndZ=0
    g2: LineSegment StartX=-530.24 StartY=826 StartZ=0 EndX=-530.24 EndY=850 EndZ=0
    g3: LineSegment StartX=-530.24 StartY=850 StartZ=0 EndX=-651.872 EndY=850 EndZ=0
  constraints (12):
    c: Coincident(g0,g1)
    c: Coincident(g1,g2)
    c: Coincident(g2,g3)
    c: Coincident(g3,g0)
    c: Vertical(g0)
    c: Vertical(g2)
    c: Horizontal(g1)
    c: Horizontal(g3)
    c: DistanceY(g-4,g1) = 1
    c: DistanceX(g2,g-4) = 15
    c: DistanceY(g2,g-4) = 15
    c: DistanceX(g-3,g0) = 15
FEATURE [PartDesign::Pocket] Pocket012
  BaseFeature = -> Pad016
  Direction = (0,0,-1)
  Length = 5
  Length2 = 5
  Placement = pos=(0,0,0) rot=(1,0,0;1.5708rad)
  Profile = -> Sketch029
  ReferenceAxis = -> Sketch029 [N_Axis]
  Refine = true
  Suppressed = false
  Type = 1
FEATURE [PartDesign::Fillet] Fillet020
  Base = -> Pocket012 [Edge4,Edge20,Edge22,Edge21]
  BaseFeature = -> Pocket012
  Placement = pos=(0,0,0) rot=(1,0,0;1.5708rad)
  Radius = 15
  Refine = true
  SupportTransform = false
  Suppressed = false
  UseAllEdges = false
FEATURE [PartDesign::Fillet] Fillet021
  Base = -> Fillet020 [Edge8,Edge10,Edge26,Edge20]
  BaseFeature = -> Fillet020
  Placement = pos=(0,0,0) rot=(1,0,0;1.5708rad)
  Radius = 5
  Refine = true
  SupportTransform = false
  Suppressed = false
  UseAllEdges = false
FEATURE [PartDesign::Body] Body011
  AllowCompound = false
  Group = -> [DatumPlane010,CopyPocket011,Sketch028,Pad016,Sketch029,Pocket012,Fillet020,Fillet021]
  Origin = -> Origin016
  Tip = -> Fillet021
PROVENANCE & LICENSES
A FreeCAD (.FCStd) document from a public repository crawl; recipes are the document's own serialized feature recipes (and, for linked parts, companion documents' recipes).
License: as declared in the source repository (recorded in the dataset sidecar).
